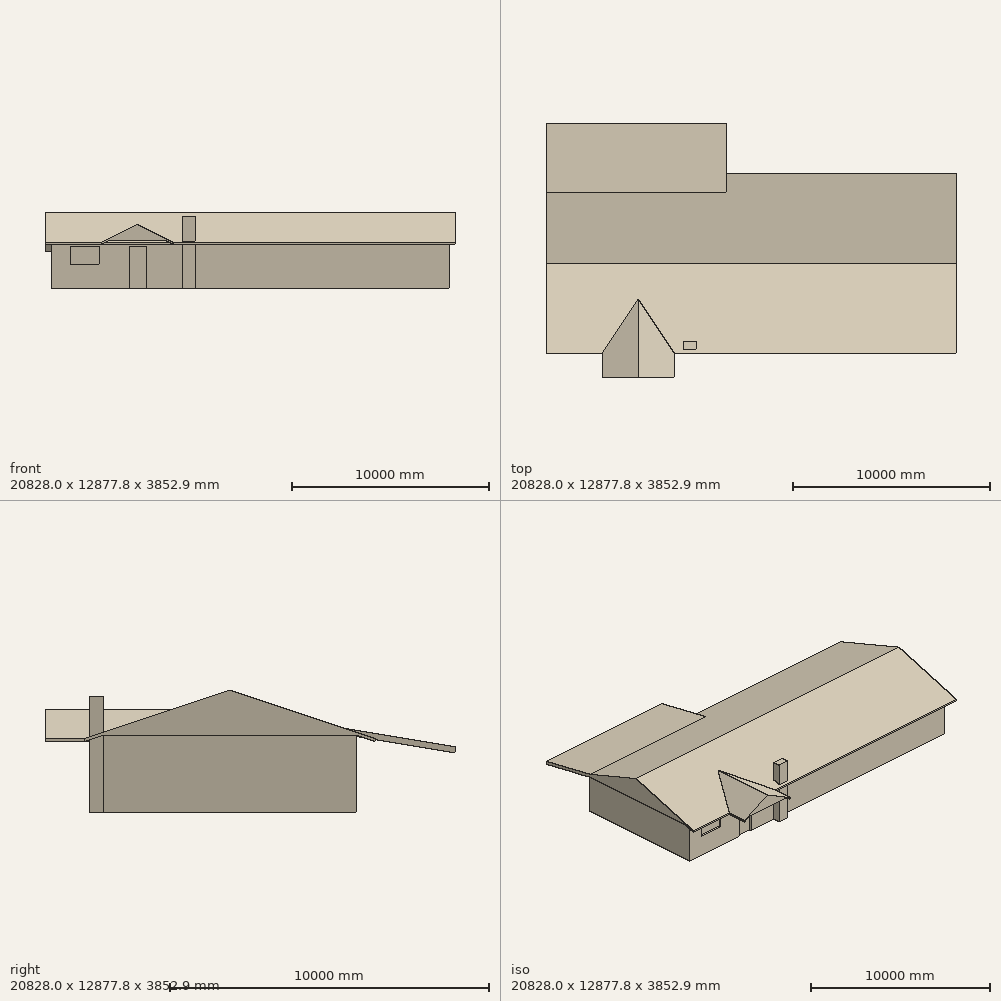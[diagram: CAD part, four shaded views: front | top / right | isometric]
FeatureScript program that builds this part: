
annotation { "Feature Type Name" : "Feature", "Feature Type Description" : "" }
export const myFeature = defineFeature(function(context is Context, id is Id, definition is map)
    precondition{}
    {
        {
            var Q0;
            Q0=qCreatedBy(makeId("Top.planeOp"),FACE);
            var sketch = newSketch(context, id + "F0", { "sketchPlane" : qUnion([Q0])});
            skLineSegment(sketch, "E0.bottom", {"start": v(0, 0) * mm, "end": v(20218.4, 0) * mm});
            skLineSegment(sketch, "E0.top", {"start": v(0, 7924.8) * mm, "end": v(20218.4, 7924.8) * mm});
            skLineSegment(sketch, "E0.left", {"start": v(0, 0) * mm, "end": v(0, 7924.8) * mm});
            skLineSegment(sketch, "E0.right", {"start": v(20218.4, 0) * mm, "end": v(20218.4, 7924.8) * mm});
            skSolve(sketch);
        }
        {
            var Q0;
            Q0 = qSketchRegion(id + "F0", true);
            extrude(context, id + "F1", {"entities" : qUnion([Q0]), "depth" : 2438.4 * mm, "offsetDistance" : 25.4 * mm});
        }
        {
            var Q0;
            Q0=makeQuery(id+"F1.opExtrude","SWEPT_FACE",FACE,{"disambiguationData":[OSD([sQuery(id+"F0.wireOp",EDGE,"E0.left")])]});
            var sketch = newSketch(context, id + "F2", { "sketchPlane" : qUnion([Q0])});
            skLineSegment(sketch, "E1", {"start": v(-8534.4, 2328.9) * mm, "end": v(-3962.4, 3852.9) * mm});
            skLineSegment(sketch, "E2", {"start": v(-3962.4, 3852.9) * mm, "end": v(609.6, 2328.9) * mm});
            skLineSegment(sketch, "E3", {"start": v(609.6, 2328.9) * mm, "end": v(609.6, 2235.2) * mm});
            skLineSegment(sketch, "E4", {"start": v(609.6, 2235.2) * mm, "end": v(0, 2438.4) * mm});
            skLineSegment(sketch, "E5", {"start": v(0, 2438.4) * mm, "end": v(-7924.8, 2438.4) * mm});
            skLineSegment(sketch, "E6", {"start": v(-7924.8, 2438.4) * mm, "end": v(-8534.4, 2235.2) * mm});
            skLineSegment(sketch, "E7", {"start": v(-8534.4, 2235.2) * mm, "end": v(-8534.4, 2328.9) * mm});
            skLineSegment(sketch, "E8", {"start": v(-3962.4, 3852.9) * mm, "end": v(-3962.4, 0) * mm, "construction": true});
            skLineSegment(sketch, "E9", {"start": v(-4267.2, 3751.3) * mm, "end": v(-3962.4, 3751.3) * mm, "construction": true});
            skLineSegment(sketch, "E10", {"start": v(-3962.4, 3751.3) * mm, "end": v(-3962.4, 3852.9) * mm, "construction": true});
            skSolve(sketch);
        }
        {
            var Q0;
            Q0 = qSketchRegion(id + "F2", true);
            extrude(context, id + "F3", {"entities" : qUnion([Q0]), "operationType" : NewBodyOperationType.ADD, "depth" : 304.8 * mm, "offsetDistance" : 25.4 * mm, "hasSecondDirection" : true, "secondDirectionOppositeDirection" : true, "secondDirectionDepth" : 20421.6 * mm + 101.6 * mm});
        }
        {
            var Q0;
            Q0=makeQuery(id+"F1.opExtrude","SWEPT_FACE",FACE,{"disambiguationData":[OSD([sQuery(id+"F0.wireOp",EDGE,"E0.bottom")])]});
            var sketch = newSketch(context, id + "F4", { "sketchPlane" : qUnion([Q0])});
            skLineSegment(sketch, "E11.bottom", {"start": v(939.8, 2133.6) * mm, "end": v(2463.8, 2133.6) * mm});
            skLineSegment(sketch, "E11.top", {"start": v(939.8, 1219.2) * mm, "end": v(2463.8, 1219.2) * mm});
            skLineSegment(sketch, "E11.left", {"start": v(939.8, 2133.6) * mm, "end": v(939.8, 1219.2) * mm});
            skLineSegment(sketch, "E11.right", {"start": v(2463.8, 2133.6) * mm, "end": v(2463.8, 1219.2) * mm});
            skLineSegment(sketch, "E12.bottom", {"start": v(3937, 2133.6) * mm, "end": v(4851.4, 2133.6) * mm});
            skLineSegment(sketch, "E12.top", {"start": v(3937, 0) * mm, "end": v(4851.4, 0) * mm});
            skLineSegment(sketch, "E12.left", {"start": v(3937, 2133.6) * mm, "end": v(3937, 0) * mm});
            skLineSegment(sketch, "E12.right", {"start": v(4851.4, 2133.6) * mm, "end": v(4851.4, 0) * mm});
            skSolve(sketch);
        }
        {
            var Q0;
            Q0 = qSketchRegion(id + "F4", true);
            extrude(context, id + "F5", {"entities" : qUnion([Q0]), "operationType" : NewBodyOperationType.REMOVE, "oppositeDirection" : true, "depth" : 101.6 * mm, "offsetDistance" : 25.4 * mm});
        }
        {
            var Q0;
            Q0=qCreatedBy(makeId("Top.planeOp"),FACE);
            var sketch = newSketch(context, id + "F6", { "sketchPlane" : qUnion([Q0])});
            skLineSegment(sketch, "E13.bottom", {"start": v(6667.5, 0) * mm, "end": v(7315.2, 0) * mm});
            skLineSegment(sketch, "E13.top", {"start": v(6667.5, -431.8) * mm, "end": v(7315.2, -431.8) * mm});
            skLineSegment(sketch, "E13.left", {"start": v(6667.5, 0) * mm, "end": v(6667.5, -431.8) * mm});
            skLineSegment(sketch, "E13.right", {"start": v(7315.2, 0) * mm, "end": v(7315.2, -431.8) * mm});
            skSolve(sketch);
        }
        {
            var Q0;
            Q0=makeQuery(id+"F6.imprint","IMPRINT",FACE,{"disambiguationData":[TD([[makeQuery(id+"F6.imprint","IMPRINT",EDGE,{"derivedFrom":sQuery(id+"F6.wireOp",EDGE,"E13.bottom")}),-1.0]])]});
            extrude(context, id + "F7", {"entities" : qUnion([Q0]), "operationType" : NewBodyOperationType.ADD, "depth" : 3657.6 * mm, "offsetDistance" : 25.4 * mm});
        }
        {
            var Q0;
            {var subQ0=sQuery(id+"F0.wireOp",EDGE,"E0.left");var subQ1=sQuery(id+"F0.wireOp",EDGE,"E0.bottom");Q0=makeQuery(id+"F7.boolean.opBoolean","SPLIT",FACE,{"disambiguationData":[TD([makeQuery(id+"F1.opExtrude","SWEPT_FACE",FACE,{"disambiguationData":[OSD([subQ0])]})])],"derivedFrom":makeQuery(id+"F1.opExtrude","SWEPT_FACE",FACE,{"disambiguationData":[OSD([subQ1])]})});}
            var sketch = newSketch(context, id + "F8", { "sketchPlane" : qUnion([Q0])});
            skLineSegment(sketch, "E14", {"start": v(2529.84, 2328.9) * mm, "end": v(4358.64, 3243.3) * mm});
            skLineSegment(sketch, "E15", {"start": v(4358.64, 3243.3) * mm, "end": v(6187.44, 2328.9) * mm});
            skLineSegment(sketch, "E16", {"start": v(6187.44, 2328.9) * mm, "end": v(6187.44, 2229.52) * mm});
            skLineSegment(sketch, "E17", {"start": v(6187.44, 2229.52) * mm, "end": v(5769.67, 2438.4) * mm});
            skLineSegment(sketch, "E18", {"start": v(5769.67, 2438.4) * mm, "end": v(2947.6, 2438.4) * mm});
            skLineSegment(sketch, "E19", {"start": v(2947.6, 2438.4) * mm, "end": v(2529.84, 2229.52) * mm});
            skLineSegment(sketch, "E20", {"start": v(2529.84, 2229.52) * mm, "end": v(2529.84, 2328.9) * mm});
            skLineSegment(sketch, "E21", {"start": v(4358.64, 2438.4) * mm, "end": v(4358.64, 3243.3) * mm, "construction": true});
            skLineSegment(sketch, "E22", {"start": v(4053.84, 3090.9) * mm, "end": v(4358.64, 3090.9) * mm, "construction": true});
            skLineSegment(sketch, "E23", {"start": v(4358.64, 3090.9) * mm, "end": v(4358.64, 3243.3) * mm, "construction": true});
            skSolve(sketch);
        }
        {
            var Q0;
            Q0 = qSketchRegion(id + "F8", true);
            var Q1;
            Q1=makeQuery(id+"F1.opExtrude","SWEPT_BODY",BODY,{"disambiguationData":[OSD([sQuery(id+"F0.wireOp",EDGE,"E0.bottom"),sQuery(id+"F0.wireOp",EDGE,"E0.top"),sQuery(id+"F0.wireOp",EDGE,"E0.left"),sQuery(id+"F0.wireOp",EDGE,"E0.right")])]});
            extrude(context, id + "F9", {"entities" : qUnion([Q0]), "operationType" : NewBodyOperationType.ADD, "depth" : 1828.8 * mm, "offsetDistance" : 25.4 * mm, "hasSecondDirection" : true, "secondDirectionBound" : SecondDirectionBoundingType.UP_TO_BODY, "secondDirectionOppositeDirection" : true, "secondDirectionDepth" : 25.4 * mm, "secondDirectionBoundEntityBody" : qUnion([Q1])});
        }
        {
            var Q0;
            Q0=makeQuery(id+"F1.opExtrude","SWEPT_FACE",FACE,{"disambiguationData":[OSD([sQuery(id+"F0.wireOp",EDGE,"E0.left")])]});
            var sketch = newSketch(context, id + "F10", { "sketchPlane" : qUnion([Q0])});
            skLineSegment(sketch, "E24", {"start": v(-7556.89, 2654.75) * mm, "end": v(-11049, 2072.73) * mm});
            skLineSegment(sketch, "E25", {"start": v(-11049, 2072.73) * mm, "end": v(-11049, 1879.6) * mm});
            skLineSegment(sketch, "E26", {"start": v(-11049, 1879.6) * mm, "end": v(-7556.89, 2461.62) * mm});
            skLineSegment(sketch, "E27", {"start": v(-7556.89, 2461.62) * mm, "end": v(-7556.89, 2654.75) * mm});
            skLineSegment(sketch, "E28", {"start": v(-11049, 1879.6) * mm, "end": v(-10744.2, 1879.6) * mm, "construction": true});
            skLineSegment(sketch, "E29", {"start": v(-10744.2, 1879.6) * mm, "end": v(-10744.2, 1930.4) * mm, "construction": true});
            skLineSegment(sketch, "E30", {"start": v(-11049, 1879.6) * mm, "end": v(-7924.8, 1879.6) * mm, "construction": true});
            skPoint(sketch, "E30.endSnap0", {"position": v(-10896.6, 1879.6) * mm});
            skLineSegment(sketch, "E31", {"start": v(-7924.8, 1879.6) * mm, "end": v(-7924.8, 2438.4) * mm, "construction": true});
            skSolve(sketch);
        }
        {
            var Q0;
            Q0 = qSketchRegion(id + "F10", true);
            var Q1;
            Q1=makeQuery(id+"F3.opExtrude","CAP_FACE",FACE,{"disambiguationData":[OSD([sQuery(id+"F2.wireOp",EDGE,"E1"),sQuery(id+"F2.wireOp",EDGE,"E2"),sQuery(id+"F2.wireOp",EDGE,"E3"),sQuery(id+"F2.wireOp",EDGE,"E4"),sQuery(id+"F2.wireOp",EDGE,"E5"),sQuery(id+"F2.wireOp",EDGE,"E6"),sQuery(id+"F2.wireOp",EDGE,"E7")])],"isStart":false});
            extrude(context, id + "F11", {"entities" : qUnion([Q0]), "operationType" : NewBodyOperationType.ADD, "endBound" : BoundingType.UP_TO_SURFACE, "depth" : 25.4 * mm, "endBoundEntityFace" : qUnion([Q1]), "offsetDistance" : 25.4 * mm, "hasSecondDirection" : true, "secondDirectionOppositeDirection" : true, "secondDirectionDepth" : 8839.2 * mm});
        }
    });
